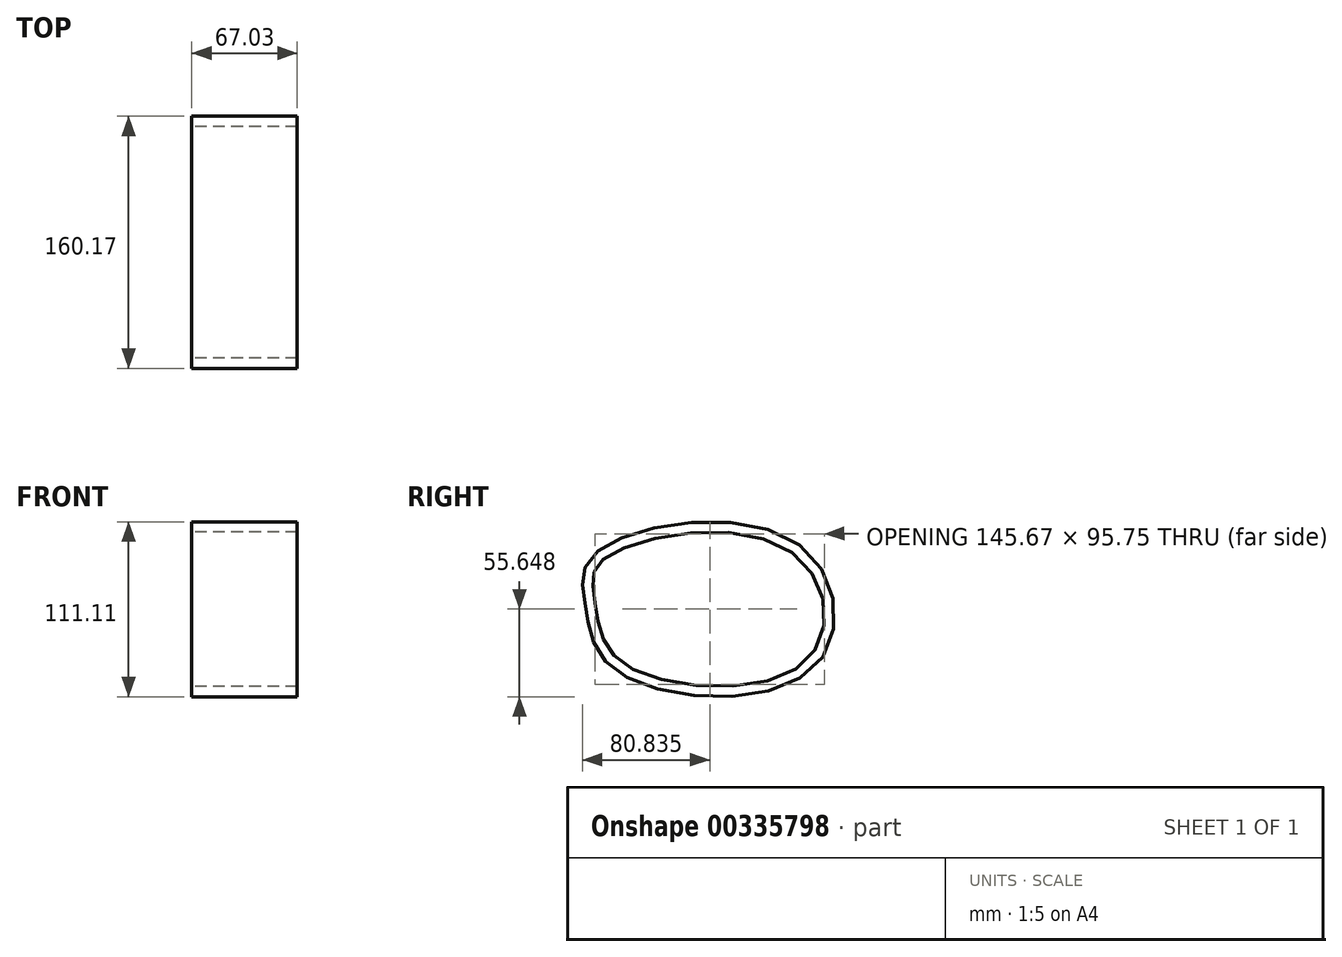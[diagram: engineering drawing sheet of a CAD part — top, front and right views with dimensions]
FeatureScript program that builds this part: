
annotation { "Feature Type Name" : "Feature", "Feature Type Description" : "" }
export const myFeature = defineFeature(function(context is Context, id is Id, definition is map)
    precondition{}
    {
        {
            var Q0;
            Q0=qCreatedBy(makeId("Top.planeOp"),FACE);
            var sketch = newSketch(context, id + "F0", { "sketchPlane" : qUnion([Q0])});
            skLineSegment(sketch, "E0.bottom", {"start": v(-32.44, 33.72) * mm, "end": v(34.6, 33.72) * mm});
            skLineSegment(sketch, "E0.top", {"start": v(-32.44, 40.25) * mm, "end": v(34.6, 40.25) * mm});
            skLineSegment(sketch, "E0.left", {"start": v(-32.44, 33.72) * mm, "end": v(-32.44, 40.25) * mm});
            skLineSegment(sketch, "E0.right", {"start": v(34.6, 33.72) * mm, "end": v(34.6, 40.25) * mm});
            skSolve(sketch);
        }
        {
            var Q0;
            Q0=qCreatedBy(makeId("Right.planeOp"),FACE);
            var sketch = newSketch(context, id + "F1", { "sketchPlane" : qUnion([Q0])});
            skFitSpline(sketch, "E1", {"points": [v(37.49, 0) * mm, v(57.12, -41.06) * mm, v(176.01, -38.92) * mm, v(164.95, 35.7) * mm, v(43.2, 29.28) * mm, v(37.49, 0) * mm]});
            skSolve(sketch);
        }
        {
            var Q0;
            Q0=makeQuery(id+"F0.imprint","IMPRINT",FACE,{"disambiguationData":[TD([[makeQuery(id+"F0.imprint","IMPRINT",EDGE,{"derivedFrom":sQuery(id+"F0.wireOp",EDGE,"E0.bottom")}),1.0]])]});
            var Q1;
            Q1=sQuery(id+"F1.wireOp",EDGE,"E1");
            sweep(context, id + "F2", {"profiles" : qUnion([Q0]), "path" : qUnion([Q1])});
        }
    });
